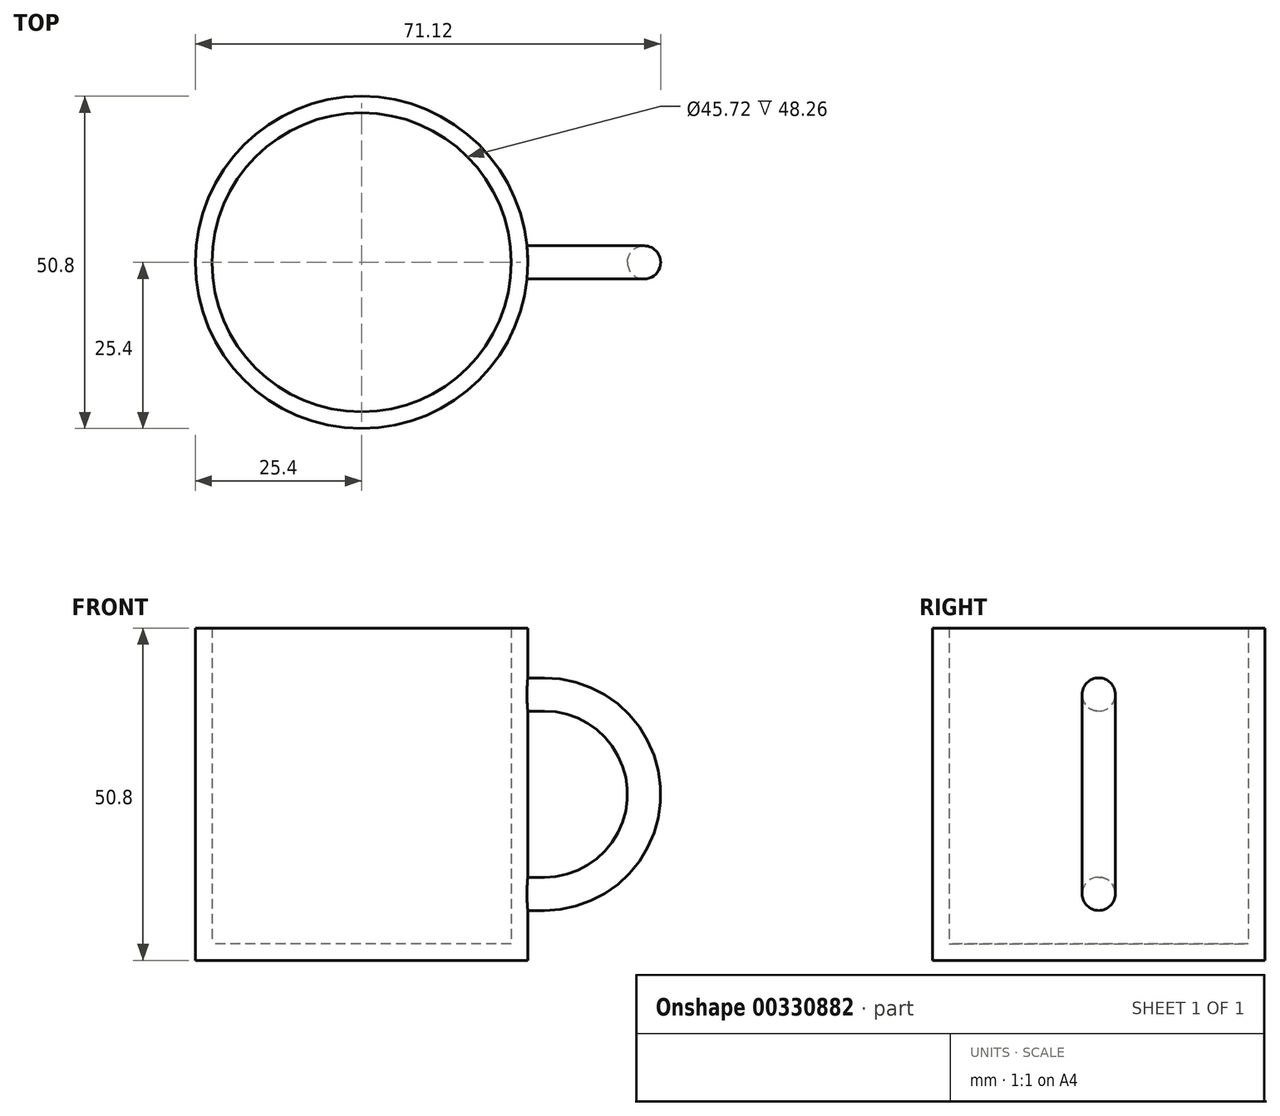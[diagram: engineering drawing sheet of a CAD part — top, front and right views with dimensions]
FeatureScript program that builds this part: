
annotation { "Feature Type Name" : "Feature", "Feature Type Description" : "" }
export const myFeature = defineFeature(function(context is Context, id is Id, definition is map)
    precondition{}
    {
        {
            var Q0;
            Q0=qCreatedBy(makeId("Top.planeOp"),FACE);
            var sketch = newSketch(context, id + "F0", { "sketchPlane" : qUnion([Q0])});
            skCircle(sketch, "E0", {"center": v(0, 0) * mm, "radius": 25.4 * mm});
            skSolve(sketch);
        }
        {
            var Q0;
            Q0=makeQuery(id+"F0.imprint","IMPRINT",FACE,{"disambiguationData":[TD([[makeQuery(id+"F0.imprint","IMPRINT",EDGE,{"derivedFrom":sQuery(id+"F0.wireOp",EDGE,"E0")}),1.0]])]});
            extrude(context, id + "F1", {"entities" : qUnion([Q0]), "endBound" : BoundingType.SYMMETRIC, "depth" : 50.8 * mm});
        }
        {
            var Q0;
            Q0=qCreatedBy(makeId("Front.planeOp"),FACE);
            var sketch = newSketch(context, id + "F2", { "sketchPlane" : qUnion([Q0])});
            skArc(sketch, "E1", {"start": v(27.94, -15.24) * mm, "mid": v(43.18, 0) * mm, "end": v(27.94, 15.24) * mm});
            skLineSegment(sketch, "E2", {"start": v(27.94, 15.24) * mm, "end": v(22.86, 15.24) * mm});
            skLineSegment(sketch, "E3", {"start": v(27.94, -15.24) * mm, "end": v(22.86, -15.24) * mm});
            skLineSegment(sketch, "E4", {"start": v(22.86, 24.23) * mm, "end": v(22.86, -19.92) * mm, "construction": true});
            skSolve(sketch);
        }
        {
            var Q0;
            Q0=qCreatedBy(makeId("Right.planeOp"),FACE);
            cPlane(context, id + "F3", {"entities" : qUnion([Q0]), "cplaneType" : CPlaneType.OFFSET, "offset" : 22.86 * mm, "width" : 152.4 * mm, "height" : 152.4 * mm});
        }
        {
            var Q0;
            Q0=qCreatedBy(id+"F3.planeOp",FACE);
            var sketch = newSketch(context, id + "F4", { "sketchPlane" : qUnion([Q0])});
            skCircle(sketch, "E5", {"center": v(0, 15.24) * mm, "radius": 2.54 * mm});
            skSolve(sketch);
        }
        {
            var Q0;
            Q0 = qSketchRegion(id + "F4", true);
            var Q1;
            Q1=sQuery(id+"F2.wireOp",EDGE,"E2");
            var Q2;
            Q2=sQuery(id+"F2.wireOp",EDGE,"E1");
            var Q3;
            Q3=sQuery(id+"F2.wireOp",EDGE,"E3");
            sweep(context, id + "F5", {"operationType" : NewBodyOperationType.ADD, "profiles" : qUnion([Q0]), "path" : qUnion([Q1, Q2, Q3])});
        }
        {
            var Q0;
            Q0=makeQuery(id+"F1.opExtrude","CAP_FACE",FACE,{"disambiguationData":[OSD([sQuery(id+"F0.wireOp",EDGE,"E0")])],"isStart":false});
            shell(context, id + "F6", {"entities" : qUnion([Q0]), "thickness" : 2.54 * mm});
        }
    });
